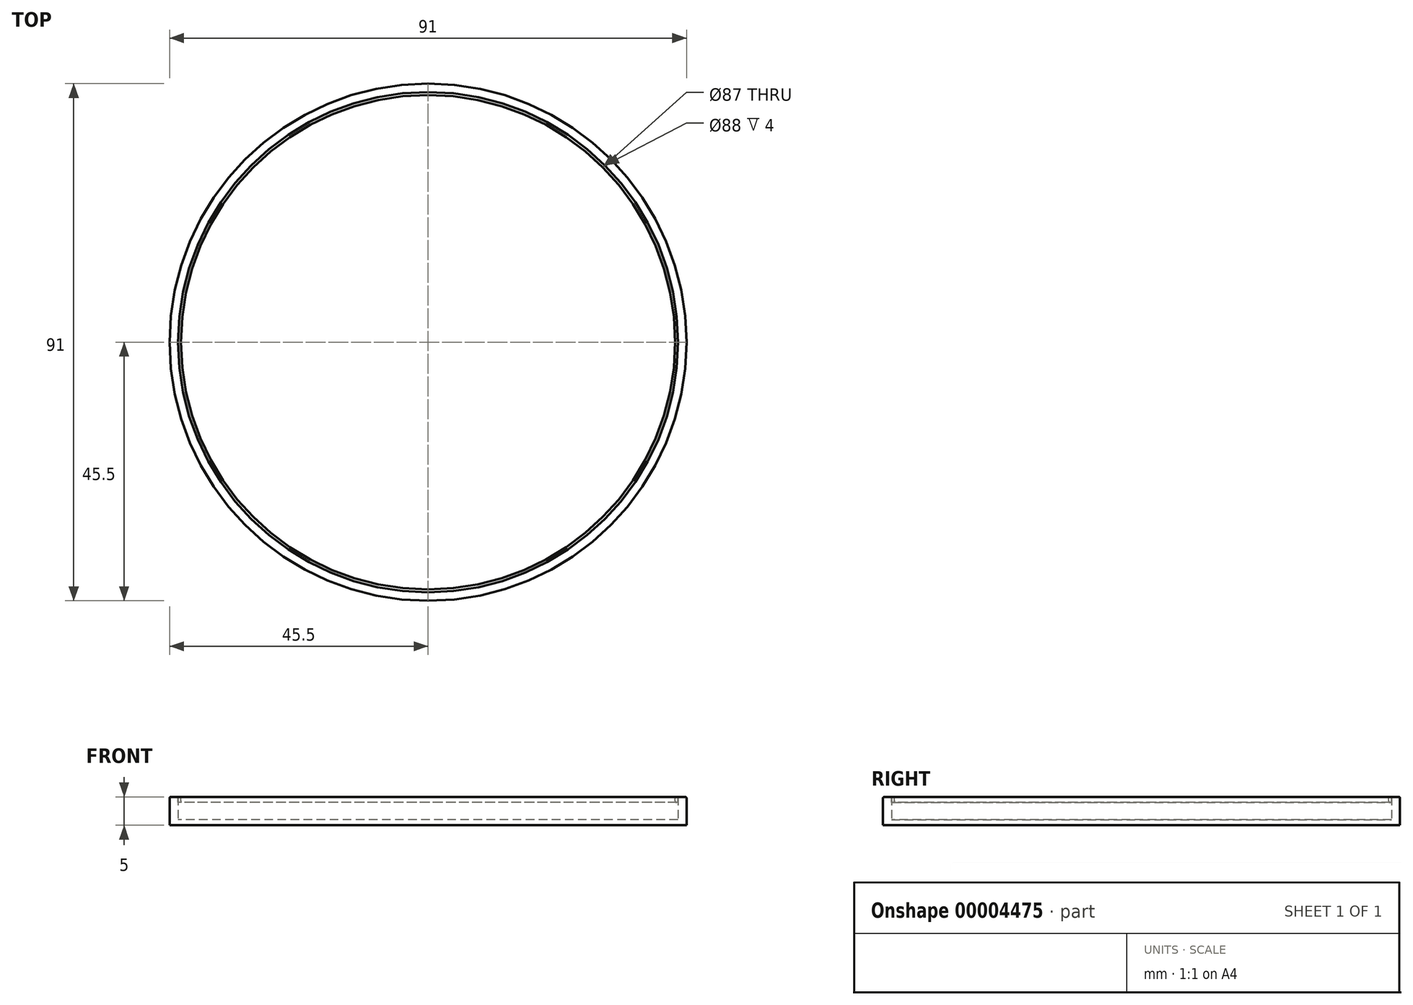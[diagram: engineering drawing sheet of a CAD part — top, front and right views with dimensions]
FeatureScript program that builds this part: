
annotation { "Feature Type Name" : "Feature", "Feature Type Description" : "" }
export const myFeature = defineFeature(function(context is Context, id is Id, definition is map)
    precondition{}
    {
        {
            var Q0;
            Q0=qCreatedBy(makeId("Top.planeOp"),FACE);
            var sketch = newSketch(context, id + "F0", { "sketchPlane" : qUnion([Q0])});
            skCircle(sketch, "E0", {"center": v(0, 0) * mm, "radius": 45.5 * mm});
            skCircle(sketch, "E1", {"center": v(0, 0) * mm, "radius": 44 * mm});
            skCircle(sketch, "E2", {"center": v(0, 0) * mm, "radius": 43.5 * mm});
            skSolve(sketch);
        }
        {
            var Q0;
            Q0=makeQuery(id+"F0.imprint","IMPRINT",FACE,{"disambiguationData":[TD([[makeQuery(id+"F0.imprint","IMPRINT",EDGE,{"derivedFrom":sQuery(id+"F0.wireOp",EDGE,"E0")}),1.0]])]});
            extrude(context, id + "F1", {"entities" : qUnion([Q0]), "depth" : 4 * mm});
        }
        {
            var Q0;
            Q0=makeQuery(id+"F1.opExtrude","CAP_FACE",FACE,{"disambiguationData":[OSD([sQuery(id+"F0.wireOp",EDGE,"E0"),sQuery(id+"F0.wireOp",EDGE,"E1")])],"isStart":false});
            var sketch = newSketch(context, id + "F2", { "sketchPlane" : qUnion([Q0])});
            skCircle(sketch, "E3.0", {"center": v(0, 0) * mm, "radius": 43.5 * mm});
            skCircle(sketch, "E4.0", {"center": v(0, 0) * mm, "radius": 45.5 * mm});
            skSolve(sketch);
        }
        {
            var Q0;
            Q0=makeQuery(id+"F2.imprint","IMPRINT",FACE,{"disambiguationData":[TD([[makeQuery(id+"F2.imprint","IMPRINT",EDGE,{"derivedFrom":sQuery(id+"F2.wireOp",EDGE,"E3.0")}),-1.0]])]});
            extrude(context, id + "F3", {"entities" : qUnion([Q0]), "oppositeDirection" : true, "depth" : 1 * mm});
        }
        {
            var Q0;
            Q0=makeQuery(id+"F3.opExtrude","CAP_EDGE",EDGE,{"disambiguationData":[OSD([sQuery(id+"F2.wireOp",EDGE,"E3.0")])],"isStart":false});
            var Q1;
            Q1=makeQuery(id+"F3.opExtrude","CAP_EDGE",EDGE,{"disambiguationData":[OSD([sQuery(id+"F2.wireOp",EDGE,"E3.0")])],"isStart":true});
            var Q2;
            Q2=makeQuery(id+"F1.opExtrude","CAP_EDGE",EDGE,{"disambiguationData":[OSD([sQuery(id+"F0.wireOp",EDGE,"E0")])],"isStart":false});
            fillet(context, id + "F4", {"entities" : qUnion([Q0, Q1, Q2]), "radius" : 0.25 * mm, "tangentPropagation" : true, "allowEdgeOverflow" : false});
        }
        {
            var Q0;
            Q0=makeQuery(id+"F0.imprint","IMPRINT",FACE,{"disambiguationData":[TD([[makeQuery(id+"F0.imprint","IMPRINT",EDGE,{"derivedFrom":sQuery(id+"F0.wireOp",EDGE,"E0")}),1.0]])]});
            var sketch = newSketch(context, id + "F5", { "sketchPlane" : qUnion([Q0])});
            skCircle(sketch, "E5.0", {"center": v(0, 0) * mm, "radius": 45.5 * mm});
            skSolve(sketch);
        }
        {
            var Q0;
            Q0=makeQuery(id+"F5.imprint","IMPRINT",FACE,{"disambiguationData":[TD([[makeQuery(id+"F5.imprint","IMPRINT",EDGE,{"derivedFrom":makeQuery(id+"F0.imprint","IMPRINT",EDGE,{"derivedFrom":sQuery(id+"F0.wireOp",EDGE,"E1")})}),1.0]])]});
            var Q1;
            Q1=makeQuery(id+"F5.imprint","IMPRINT",FACE,{"disambiguationData":[TD([[makeQuery(id+"F5.imprint","IMPRINT",EDGE,{"derivedFrom":sQuery(id+"F5.wireOp",EDGE,"E5.0")}),1.0]])]});
            extrude(context, id + "F6", {"entities" : qUnion([Q0, Q1]), "operationType" : NewBodyOperationType.ADD, "oppositeDirection" : true, "depth" : 1 * mm});
        }
    });
